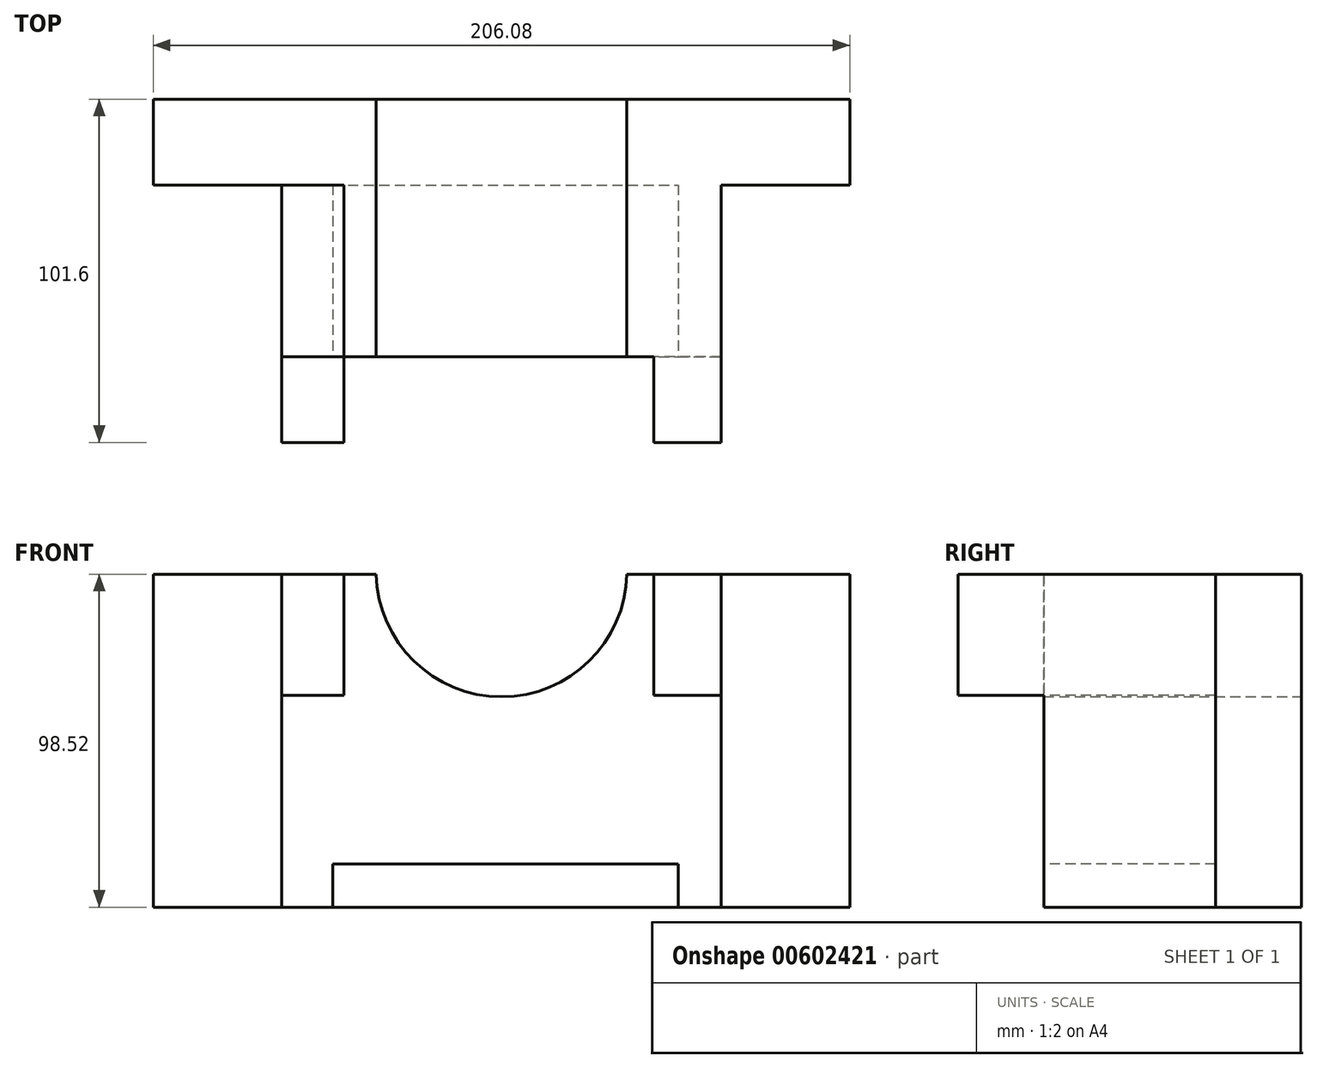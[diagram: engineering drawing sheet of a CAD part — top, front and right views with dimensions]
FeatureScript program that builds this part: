
annotation { "Feature Type Name" : "Feature", "Feature Type Description" : "" }
export const myFeature = defineFeature(function(context is Context, id is Id, definition is map)
    precondition{}
    {
        {
            var Q0;
            Q0=qCreatedBy(makeId("Front.planeOp"),FACE);
            var sketch = newSketch(context, id + "F0", { "sketchPlane" : qUnion([Q0])});
            skLineSegment(sketch, "E0.bottom", {"start": v(-103.04, 49.26) * mm, "end": v(103.04, 49.26) * mm});
            skLineSegment(sketch, "E0.top", {"start": v(-103.04, -49.26) * mm, "end": v(103.04, -49.26) * mm});
            skLineSegment(sketch, "E0.left", {"start": v(-103.04, 49.26) * mm, "end": v(-103.04, -49.26) * mm});
            skLineSegment(sketch, "E0.right", {"start": v(103.04, 49.26) * mm, "end": v(103.04, -49.26) * mm});
            skPoint(sketch, "E0.middle", {"position": v(0, 0) * mm});
            skSolve(sketch);
        }
        {
            var Q0;
            Q0=makeQuery(id+"F0.imprint","IMPRINT",FACE,{"disambiguationData":[TD([[makeQuery(id+"F0.imprint","IMPRINT",EDGE,{"derivedFrom":sQuery(id+"F0.wireOp",EDGE,"E0.bottom")}),-1.0]])]});
            extrude(context, id + "F1", {"entities" : qUnion([Q0]), "depth" : 25.4 * mm, "offsetDistance" : 25.4 * mm});
        }
        {
            var Q0;
            Q0=makeQuery(id+"F1.opExtrude","CAP_FACE",FACE,{"disambiguationData":[OSD([sQuery(id+"F0.wireOp",EDGE,"E0.bottom"),sQuery(id+"F0.wireOp",EDGE,"E0.top"),sQuery(id+"F0.wireOp",EDGE,"E0.left"),sQuery(id+"F0.wireOp",EDGE,"E0.right")])],"isStart":false});
            var sketch = newSketch(context, id + "F2", { "sketchPlane" : qUnion([Q0])});
            skLineSegment(sketch, "E1.bottom", {"start": v(-65.03, 49.26) * mm, "end": v(65.03, 49.26) * mm});
            skLineSegment(sketch, "E1.top", {"start": v(-65.03, -49.26) * mm, "end": v(65.03, -49.26) * mm});
            skLineSegment(sketch, "E1.left", {"start": v(-65.03, 49.26) * mm, "end": v(-65.03, -49.26) * mm});
            skLineSegment(sketch, "E1.right", {"start": v(65.03, 49.26) * mm, "end": v(65.03, -49.26) * mm});
            skPoint(sketch, "E1.middle", {"position": v(0, 0) * mm});
            skSolve(sketch);
        }
        {
            var Q0;
            Q0=makeQuery(id+"F2.imprint","IMPRINT",FACE,{"disambiguationData":[TD([[makeQuery(id+"F2.imprint","IMPRINT",EDGE,{"derivedFrom":sQuery(id+"F2.wireOp",EDGE,"E1.bottom")}),-1.0]])]});
            extrude(context, id + "F3", {"entities" : qUnion([Q0]), "operationType" : NewBodyOperationType.ADD, "depth" : 50.8 * mm, "offsetDistance" : 25.4 * mm});
        }
        {
            var Q0;
            Q0=makeQuery(id+"F3.opExtrude","CAP_FACE",FACE,{"disambiguationData":[OSD([sQuery(id+"F2.wireOp",EDGE,"E1.bottom"),sQuery(id+"F2.wireOp",EDGE,"E1.top"),sQuery(id+"F2.wireOp",EDGE,"E1.left"),sQuery(id+"F2.wireOp",EDGE,"E1.right")])],"isStart":false});
            var sketch = newSketch(context, id + "F4", { "sketchPlane" : qUnion([Q0])});
            skLineSegment(sketch, "E2.bottom", {"start": v(-49.99, -49.26) * mm, "end": v(52.32, -49.26) * mm});
            skLineSegment(sketch, "E2.top", {"start": v(-49.99, -36.43) * mm, "end": v(52.32, -36.43) * mm});
            skLineSegment(sketch, "E2.left", {"start": v(-49.99, -49.26) * mm, "end": v(-49.99, -36.43) * mm});
            skLineSegment(sketch, "E2.right", {"start": v(52.32, -49.26) * mm, "end": v(52.32, -36.43) * mm});
            skCircle(sketch, "E3", {"center": v(0, 49.26) * mm, "radius": 31.26 * mm});
            skSolve(sketch);
        }
        {
            var Q0;
            Q0=makeQuery(id+"F4.imprint","IMPRINT",FACE,{"disambiguationData":[TD([[makeQuery(id+"F4.imprint","IMPRINT",EDGE,{"derivedFrom":sQuery(id+"F4.wireOp",EDGE,"E2.bottom")}),1.0]])]});
            extrude(context, id + "F5", {"entities" : qUnion([Q0]), "operationType" : NewBodyOperationType.REMOVE, "oppositeDirection" : true, "depth" : 50.8 * mm, "offsetDistance" : 25.4 * mm});
        }
        {
            var Q0;
            Q0=qCreatedBy(makeId("Front.planeOp"),FACE);
            var sketch = newSketch(context, id + "F6", { "sketchPlane" : qUnion([Q0])});
            skCircle(sketch, "E4", {"center": v(0, 50.11) * mm, "radius": 37.1 * mm});
            skSolve(sketch);
        }
        {
            var Q0;
            Q0=makeQuery(id+"F6.imprint","IMPRINT",FACE,{"disambiguationData":[TD([[makeQuery(id+"F6.imprint","IMPRINT",EDGE,{"derivedFrom":sQuery(id+"F6.wireOp",EDGE,"E4")}),1.0]])]});
            extrude(context, id + "F7", {"entities" : qUnion([Q0]), "operationType" : NewBodyOperationType.REMOVE, "depth" : 76.2 * mm, "offsetDistance" : 25.4 * mm});
        }
        {
            var Q0;
            Q0=makeQuery(id+"F3.opExtrude","CAP_FACE",FACE,{"disambiguationData":[OSD([sQuery(id+"F2.wireOp",EDGE,"E1.bottom"),sQuery(id+"F2.wireOp",EDGE,"E1.top"),sQuery(id+"F2.wireOp",EDGE,"E1.left"),sQuery(id+"F2.wireOp",EDGE,"E1.right")])],"isStart":false});
            var sketch = newSketch(context, id + "F8", { "sketchPlane" : qUnion([Q0])});
            skLineSegment(sketch, "E5.bottom", {"start": v(-65.03, 49.26) * mm, "end": v(-46.7, 49.26) * mm});
            skLineSegment(sketch, "E5.top", {"start": v(-65.03, 13.45) * mm, "end": v(-46.7, 13.45) * mm});
            skLineSegment(sketch, "E5.left", {"start": v(-65.03, 49.26) * mm, "end": v(-65.03, 13.45) * mm});
            skLineSegment(sketch, "E5.right", {"start": v(-46.7, 49.26) * mm, "end": v(-46.7, 13.45) * mm});
            skLineSegment(sketch, "E6.bottom", {"start": v(65.03, 49.26) * mm, "end": v(45.07, 49.26) * mm});
            skLineSegment(sketch, "E6.top", {"start": v(65.03, 13.45) * mm, "end": v(45.07, 13.45) * mm});
            skLineSegment(sketch, "E6.left", {"start": v(65.03, 49.26) * mm, "end": v(65.03, 13.45) * mm});
            skLineSegment(sketch, "E6.right", {"start": v(45.07, 49.26) * mm, "end": v(45.07, 13.45) * mm});
            skSolve(sketch);
        }
        {
            var Q0;
            Q0=makeQuery(id+"F8.imprint","IMPRINT",FACE,{"disambiguationData":[TD([[makeQuery(id+"F8.imprint","IMPRINT",EDGE,{"derivedFrom":sQuery(id+"F8.wireOp",EDGE,"E5.bottom")}),-1.0]])]});
            extrude(context, id + "F9", {"entities" : qUnion([Q0]), "operationType" : NewBodyOperationType.REMOVE, "oppositeDirection" : true, "depth" : 50.8 * mm, "offsetDistance" : 25.4 * mm});
        }
        {
            var Q0;
            Q0 = qSketchRegion(id + "F8", true);
            extrude(context, id + "F10", {"entities" : qUnion([Q0]), "operationType" : NewBodyOperationType.ADD, "depth" : 25.4 * mm, "offsetDistance" : 25.4 * mm});
        }
    });
